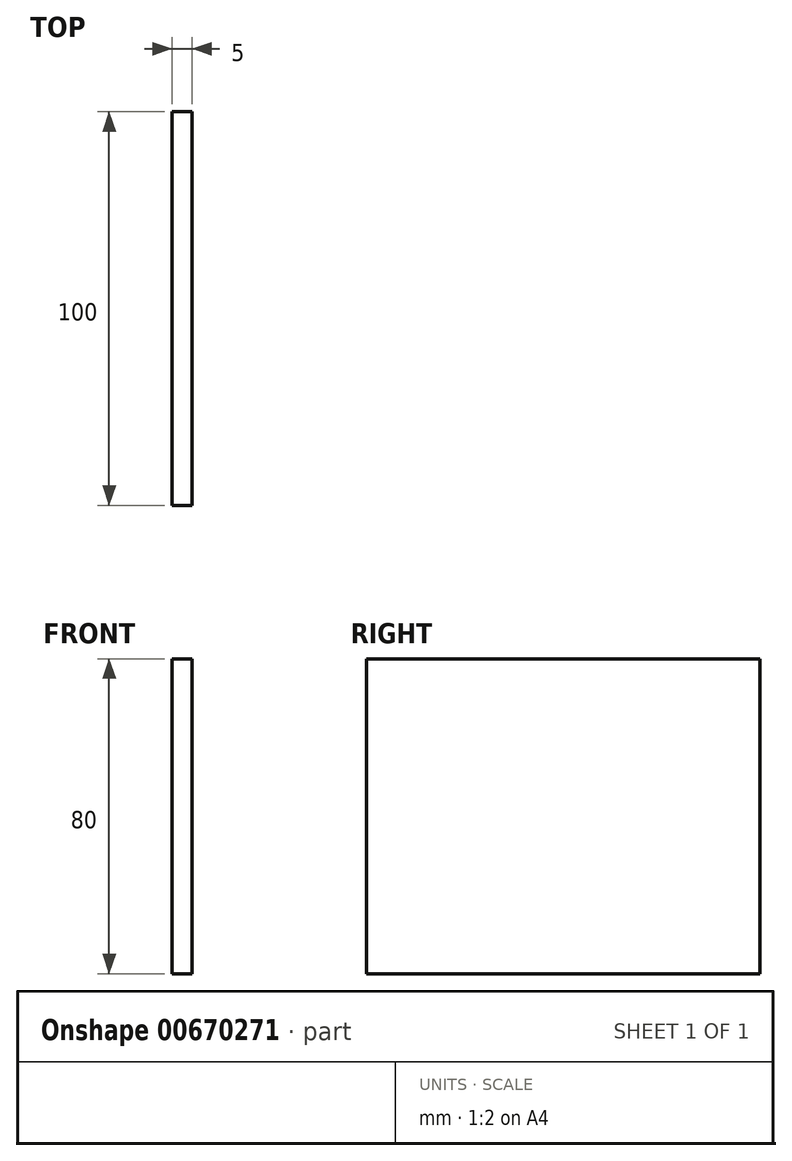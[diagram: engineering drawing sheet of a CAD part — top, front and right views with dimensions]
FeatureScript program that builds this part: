
annotation { "Feature Type Name" : "Feature", "Feature Type Description" : "" }
export const myFeature = defineFeature(function(context is Context, id is Id, definition is map)
    precondition{}
    {
        {
            var Q0;
            Q0=qCreatedBy(makeId("Right.planeOp"),FACE);
            var sketch = newSketch(context, id + "F0", { "sketchPlane" : qUnion([Q0])});
            skLineSegment(sketch, "E0.bottom", {"start": v(-47.11, 46.03) * mm, "end": v(52.89, 46.03) * mm});
            skLineSegment(sketch, "E0.top", {"start": v(-47.11, -33.97) * mm, "end": v(52.89, -33.97) * mm});
            skLineSegment(sketch, "E0.left", {"start": v(-47.11, 46.03) * mm, "end": v(-47.11, -33.97) * mm});
            skLineSegment(sketch, "E0.right", {"start": v(52.89, 46.03) * mm, "end": v(52.89, -33.97) * mm});
            skSolve(sketch);
        }
        {
            var Q0;
            Q0=makeQuery(id+"F0.imprint","IMPRINT",FACE,{"disambiguationData":[TD([[makeQuery(id+"F0.imprint","IMPRINT",EDGE,{"derivedFrom":sQuery(id+"F0.wireOp",EDGE,"E0.bottom")}),-1.0]])]});
            extrude(context, id + "F1", {"entities" : qUnion([Q0]), "depth" : 5 * mm, "offsetDistance" : 25 * mm});
        }
    });
